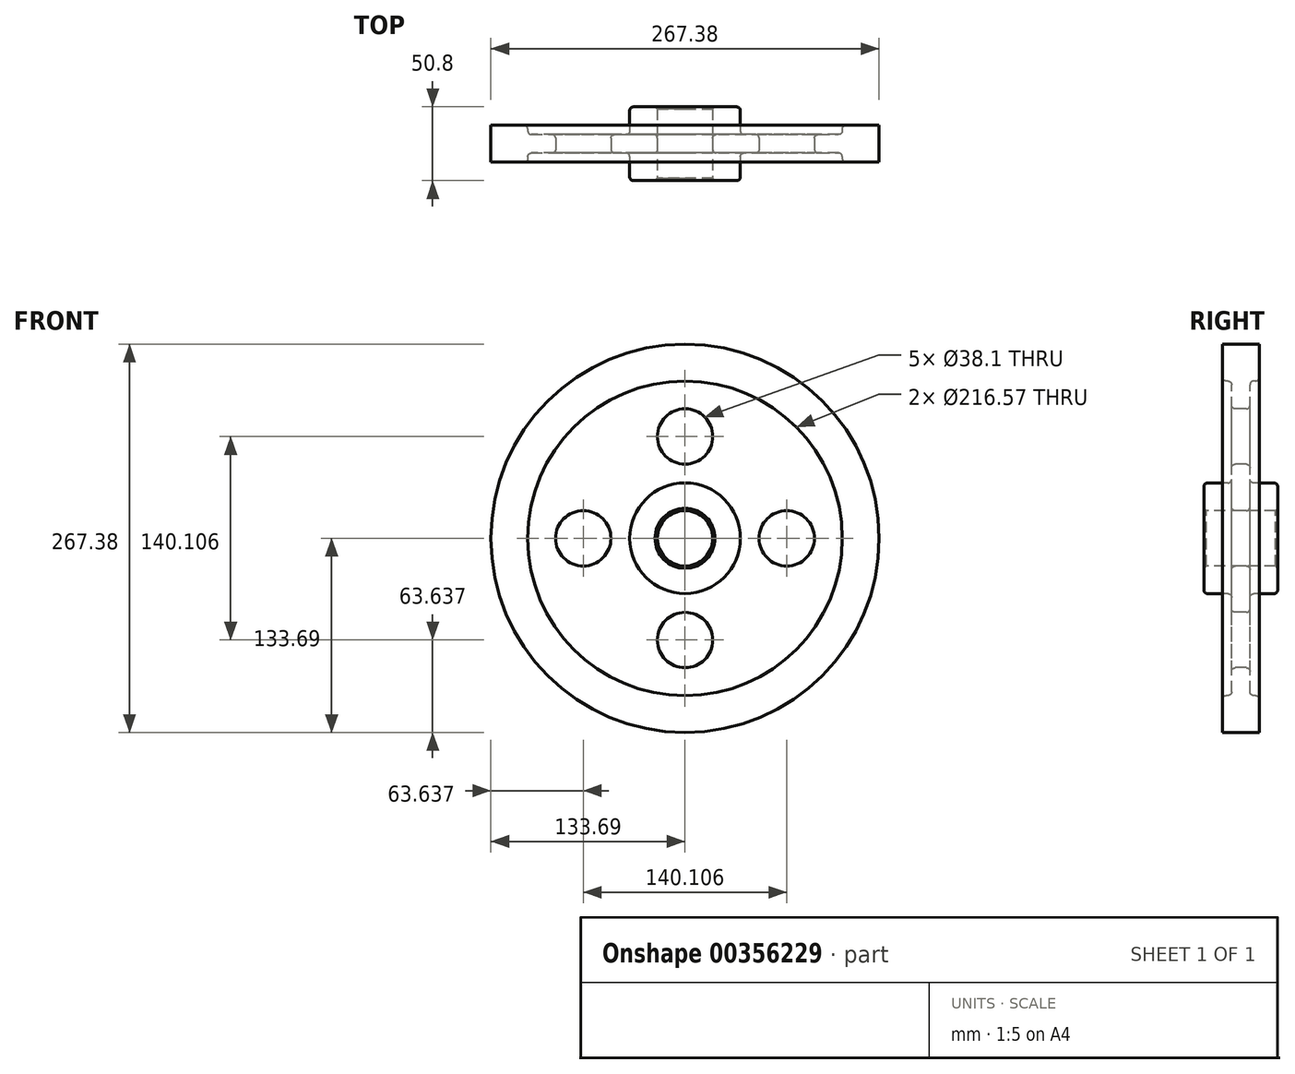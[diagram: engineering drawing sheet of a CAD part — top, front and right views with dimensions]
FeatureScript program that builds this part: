
annotation { "Feature Type Name" : "Feature", "Feature Type Description" : "" }
export const myFeature = defineFeature(function(context is Context, id is Id, definition is map)
    precondition{}
    {
        {
            var Q0;
            Q0=qCreatedBy(makeId("Right.planeOp"),FACE);
            var sketch = newSketch(context, id + "F0", { "sketchPlane" : qUnion([Q0])});
            skLineSegment(sketch, "E0", {"start": v(0, 0) * mm, "end": v(0, 28.58) * mm});
            skLineSegment(sketch, "E1", {"start": v(0, 28.58) * mm, "end": v(0, 73.03) * mm});
            skLineSegment(sketch, "E2", {"start": v(0, 73.03) * mm, "end": v(0, 120.99) * mm});
            skLineSegment(sketch, "E3.bottom", {"start": v(25.4, 19.05) * mm, "end": v(-25.4, 19.05) * mm});
            skLineSegment(sketch, "E3.top", {"start": v(25.4, 38.1) * mm, "end": v(6.35, 38.1) * mm});
            skLineSegment(sketch, "E3.left", {"start": v(25.4, 19.05) * mm, "end": v(25.4, 38.1) * mm});
            skLineSegment(sketch, "E3.right", {"start": v(-25.4, 19.05) * mm, "end": v(-25.4, 38.1) * mm});
            skPoint(sketch, "E3.middle", {"position": v(0, 28.58) * mm});
            skLineSegment(sketch, "E4.bottom", {"start": v(12.7, 108.29) * mm, "end": v(6.35, 108.29) * mm});
            skLineSegment(sketch, "E4.top", {"start": v(12.7, 133.69) * mm, "end": v(-12.7, 133.69) * mm});
            skLineSegment(sketch, "E4.left", {"start": v(12.7, 108.29) * mm, "end": v(12.7, 133.69) * mm});
            skLineSegment(sketch, "E4.right", {"start": v(-12.7, 108.29) * mm, "end": v(-12.7, 133.69) * mm});
            skPoint(sketch, "E4.middle", {"position": v(0, 120.99) * mm});
            skLineSegment(sketch, "E5.left", {"start": v(6.35, 31.44) * mm, "end": v(6.35, 114.6) * mm});
            skLineSegment(sketch, "E5.right", {"start": v(-6.35, 31.44) * mm, "end": v(-6.35, 114.6) * mm});
            skPoint(sketch, "E5.middle", {"position": v(0, 73.03) * mm});
            skLineSegment(sketch, "E6.trimOffspring", {"start": v(-6.35, 108.29) * mm, "end": v(-12.7, 108.29) * mm});
            skLineSegment(sketch, "E7.trimOffspring", {"start": v(-6.35, 38.1) * mm, "end": v(-25.4, 38.1) * mm});
            skLineSegment(sketch, "E8", {"start": v(0, 0) * mm, "end": v(81.33, 0) * mm});
            skSolve(sketch);
        }
        {
            var Q0;
            {var subQ4=sQuery(id+"F0.wireOp",EDGE,"E3.top");Q0=makeQuery(id+"F0.imprint","IMPRINT",FACE,{"disambiguationData":[TD([[makeQuery(id+"F0.imprint","IMPRINT",EDGE,{"derivedFrom":subQ4}),1.0]])]});}
            var Q1;
            Q1=sQuery(id+"F0.wireOp",EDGE,"E8");
            revolve(context, id + "F1", {"entities" : qUnion([Q0]), "axis" : qUnion([Q1]), "revolveType" : RevolveType.FULL});
        }
        {
            var Q0;
            Q0=makeQuery(id+"F1.opRevolve","SWEPT_FACE",FACE,{"disambiguationData":[OSD([sQuery(id+"F0.wireOp",EDGE,"E5.right")])]});
            var sketch = newSketch(context, id + "F2", { "sketchPlane" : qUnion([Q0])});
            skLineSegment(sketch, "E9", {"start": v(0, 0) * mm, "end": v(0, 70.05) * mm});
            skCircle(sketch, "E10", {"center": v(0, 70.05) * mm, "radius": 19.05 * mm});
            skCircle(sketch, "E11.1.0", {"center": v(-70.05, 0) * mm, "radius": 19.05 * mm});
            skCircle(sketch, "E11.2.0", {"center": v(0, -70.05) * mm, "radius": 19.05 * mm});
            skCircle(sketch, "E11.3.0", {"center": v(70.05, 0) * mm, "radius": 19.05 * mm});
            skPoint(sketch, "E11.center", {"position": v(0, 0) * mm});
            skSolve(sketch);
        }
        {
            var Q0;
            Q0=makeQuery(id+"F2.imprint","IMPRINT",FACE,{"disambiguationData":[TD([[makeQuery(id+"F2.imprint","IMPRINT",EDGE,{"derivedFrom":sQuery(id+"F2.wireOp",EDGE,"E11.3.0")}),1.0]])]});
            var Q1;
            Q1=makeQuery(id+"F2.imprint","IMPRINT",FACE,{"disambiguationData":[TD([[makeQuery(id+"F2.imprint","IMPRINT",EDGE,{"derivedFrom":sQuery(id+"F2.wireOp",EDGE,"E11.2.0")}),1.0]])]});
            var Q2;
            Q2=makeQuery(id+"F2.imprint","IMPRINT",FACE,{"disambiguationData":[TD([[makeQuery(id+"F2.imprint","IMPRINT",EDGE,{"derivedFrom":sQuery(id+"F2.wireOp",EDGE,"E11.1.0")}),1.0]])]});
            var Q3;
            Q3=makeQuery(id+"F2.imprint","IMPRINT",FACE,{"disambiguationData":[TD([[makeQuery(id+"F2.imprint","IMPRINT",EDGE,{"derivedFrom":sQuery(id+"F2.wireOp",EDGE,"E10")}),1.0]])]});
            extrude(context, id + "F3", {"entities" : qUnion([Q0, Q1, Q2, Q3]), "operationType" : NewBodyOperationType.REMOVE, "oppositeDirection" : true, "depth" : 25.4 * mm});
        }
        {
            var Q0;
            Q0=makeQuery(id+"F1.opRevolve","SWEPT_EDGE",EDGE,{"disambiguationData":[OSD([sQuery(id+"F0.wireOp",EDGE,"E3.top"),sQuery(id+"F0.wireOp",EDGE,"E3.left")])]});
            var Q1;
            Q1=makeQuery(id+"F1.opRevolve","SWEPT_EDGE",EDGE,{"disambiguationData":[OSD([sQuery(id+"F0.wireOp",EDGE,"E3.top"),sQuery(id+"F0.wireOp",EDGE,"E5.left")])]});
            var Q2;
            Q2=makeQuery(id+"F1.opRevolve","SWEPT_EDGE",EDGE,{"disambiguationData":[OSD([sQuery(id+"F0.wireOp",EDGE,"E4.bottom"),sQuery(id+"F0.wireOp",EDGE,"E4.left")])]});
            var Q3;
            Q3=makeQuery(id+"F1.opRevolve","SWEPT_FACE",FACE,{"disambiguationData":[OSD([sQuery(id+"F0.wireOp",EDGE,"E5.left")])]});
            var Q4;
            Q4=makeQuery(id+"F1.opRevolve","SWEPT_EDGE",EDGE,{"disambiguationData":[OSD([sQuery(id+"F0.wireOp",EDGE,"E3.right"),sQuery(id+"F0.wireOp",EDGE,"E7.trimOffspring")])]});
            var Q5;
            Q5=makeQuery(id+"F1.opRevolve","SWEPT_EDGE",EDGE,{"disambiguationData":[OSD([sQuery(id+"F0.wireOp",EDGE,"E5.right"),sQuery(id+"F0.wireOp",EDGE,"E7.trimOffspring")])]});
            var Q6;
            Q6=makeQuery(id+"F1.opRevolve","SWEPT_EDGE",EDGE,{"disambiguationData":[OSD([sQuery(id+"F0.wireOp",EDGE,"E4.right"),sQuery(id+"F0.wireOp",EDGE,"E6.trimOffspring")])]});
            var Q7;
            Q7=makeQuery(id+"F1.opRevolve","SWEPT_FACE",FACE,{"disambiguationData":[OSD([sQuery(id+"F0.wireOp",EDGE,"E5.right")])]});
            fillet(context, id + "F4", {"entities" : qUnion([Q0, Q1, Q2, Q3, Q4, Q5, Q6, Q7]), "radius" : 2.54 * mm, "tangentPropagation" : true, "allowEdgeOverflow" : false});
        }
        {
            var Q0;
            Q0=makeQuery(id+"F1.opRevolve","SWEPT_EDGE",EDGE,{"disambiguationData":[OSD([sQuery(id+"F0.wireOp",EDGE,"E3.bottom"),sQuery(id+"F0.wireOp",EDGE,"E3.right")])]});
            var Q1;
            Q1=makeQuery(id+"F1.opRevolve","SWEPT_EDGE",EDGE,{"disambiguationData":[OSD([sQuery(id+"F0.wireOp",EDGE,"E3.bottom"),sQuery(id+"F0.wireOp",EDGE,"E3.left")])]});
            chamfer(context, id + "F5", {"entities" : qUnion([Q0, Q1]), "width" : 1.59 * mm, "tangentPropagation" : true});
        }
    });
